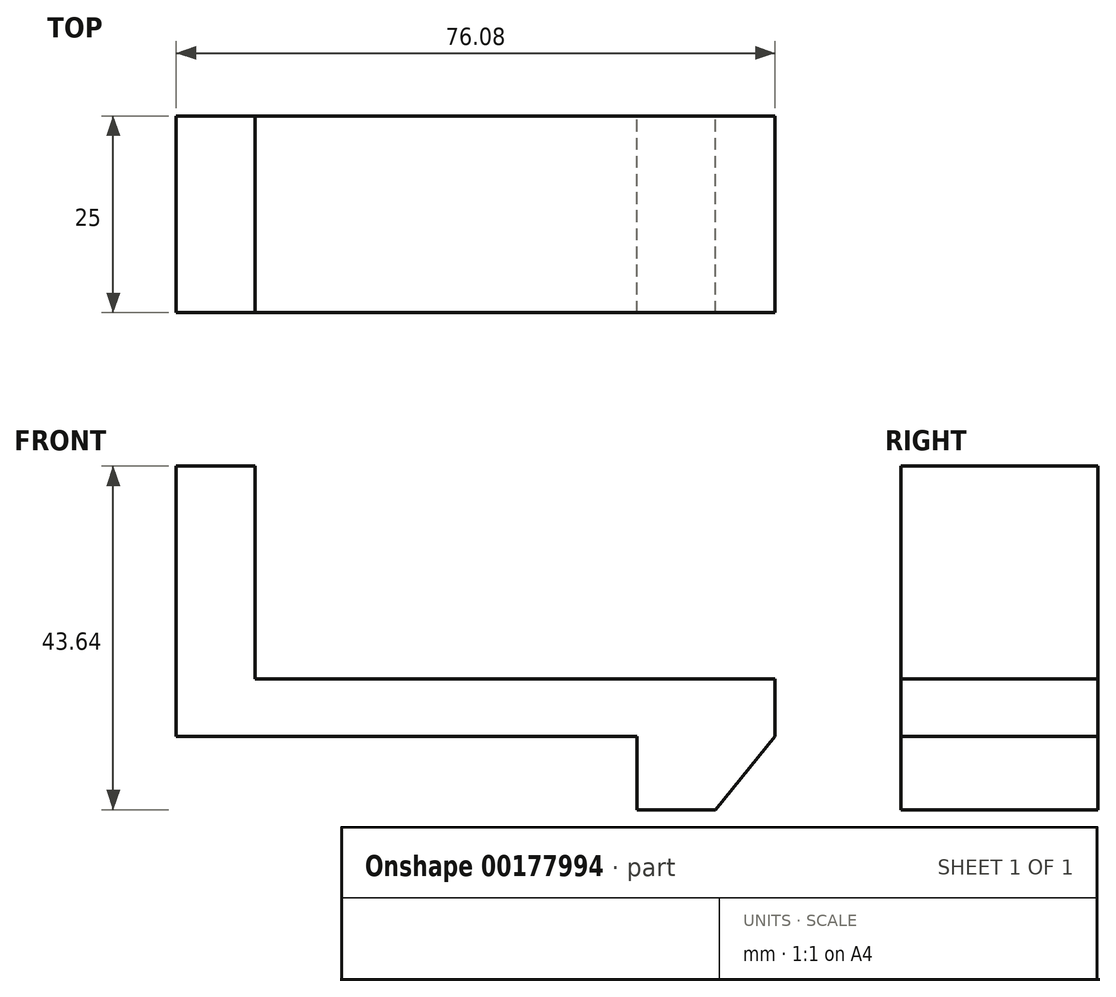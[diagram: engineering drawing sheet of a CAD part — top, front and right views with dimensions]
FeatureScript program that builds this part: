
annotation { "Feature Type Name" : "Feature", "Feature Type Description" : "" }
export const myFeature = defineFeature(function(context is Context, id is Id, definition is map)
    precondition{}
    {
        {
            var Q0;
            Q0=qCreatedBy(makeId("Front.planeOp"),FACE);
            var sketch = newSketch(context, id + "F0", { "sketchPlane" : qUnion([Q0])});
            skLineSegment(sketch, "E0.bottom", {"start": v(38.04, 3.63) * mm, "end": v(-28.04, 3.63) * mm});
            skLineSegment(sketch, "E0.top", {"start": v(38.04, -3.63) * mm, "end": v(-38.04, -3.63) * mm});
            skLineSegment(sketch, "E0.left", {"start": v(38.04, 3.63) * mm, "end": v(38.04, -3.63) * mm});
            skLineSegment(sketch, "E0.right", {"start": v(-38.04, 3.63) * mm, "end": v(-38.04, -3.63) * mm});
            skPoint(sketch, "E0.middle", {"position": v(0, 0) * mm});
            skLineSegment(sketch, "E1", {"start": v(-38.04, 3.63) * mm, "end": v(-38.04, 30.69) * mm});
            skLineSegment(sketch, "E2", {"start": v(-38.04, 30.69) * mm, "end": v(-28.04, 30.69) * mm});
            skLineSegment(sketch, "E3", {"start": v(-28.04, 30.69) * mm, "end": v(-28.04, 3.63) * mm});
            skLineSegment(sketch, "E4", {"start": v(38.04, -3.63) * mm, "end": v(30.48, -12.95) * mm});
            skLineSegment(sketch, "E5", {"start": v(30.48, -12.95) * mm, "end": v(20.48, -12.95) * mm});
            skLineSegment(sketch, "E6", {"start": v(20.48, -12.95) * mm, "end": v(20.48, -3.63) * mm});
            skSolve(sketch);
        }
        {
            var Q0;
            Q0 = qSketchRegion(id + "F0", true);
            extrude(context, id + "F1", {"entities" : qUnion([Q0]), "depth" : 25 * mm});
        }
    });
